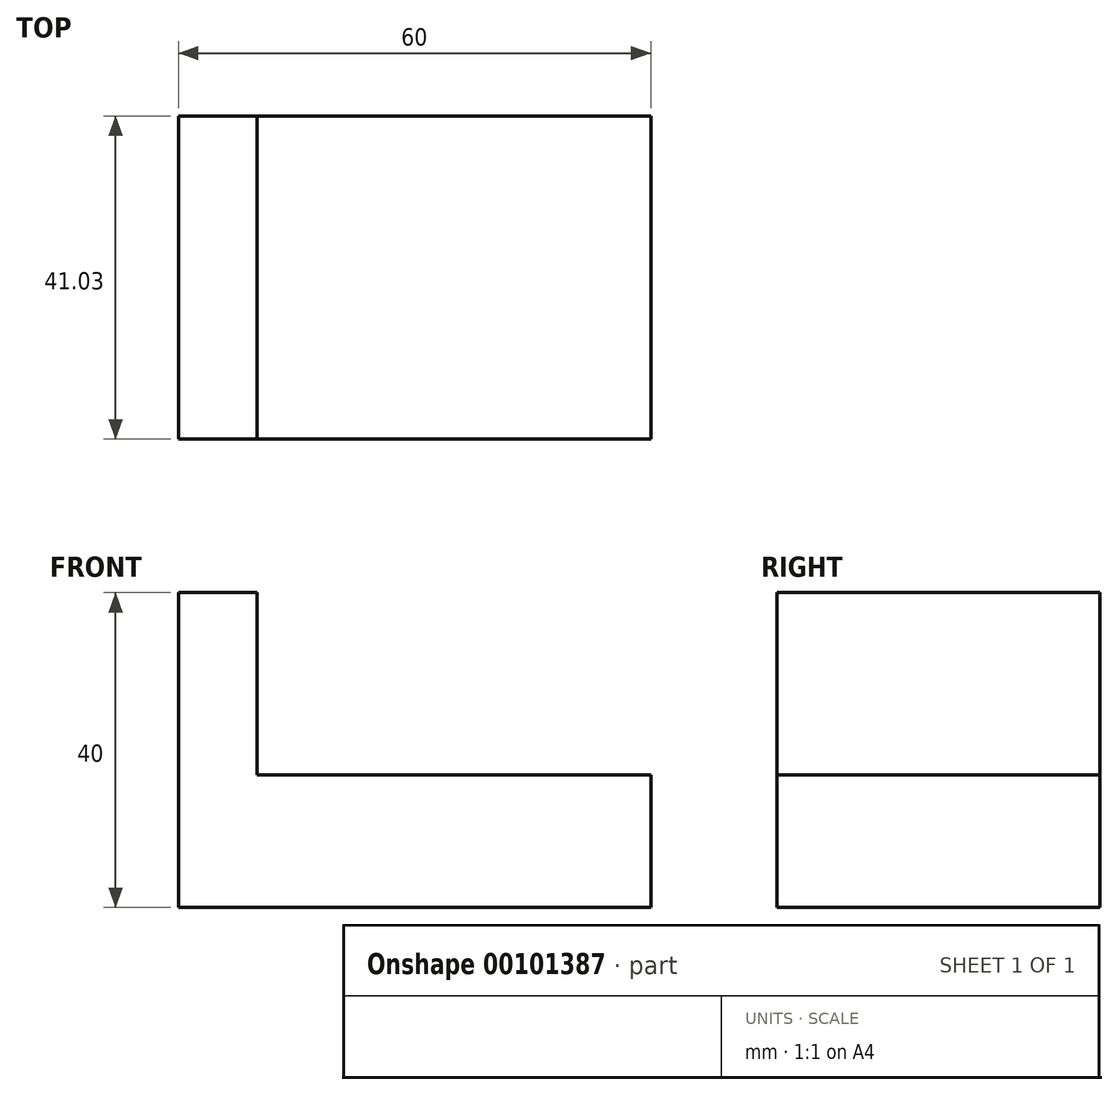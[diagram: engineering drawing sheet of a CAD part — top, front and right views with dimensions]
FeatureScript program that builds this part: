
annotation { "Feature Type Name" : "Feature", "Feature Type Description" : "" }
export const myFeature = defineFeature(function(context is Context, id is Id, definition is map)
    precondition{}
    {
        {
            var Q0;
            Q0=qCreatedBy(makeId("Front.planeOp"),FACE);
            var sketch = newSketch(context, id + "F0", { "sketchPlane" : qUnion([Q0])});
            skLineSegment(sketch, "E0", {"start": v(0, 0) * mm, "end": v(0, 40) * mm});
            skLineSegment(sketch, "E1", {"start": v(0, 40) * mm, "end": v(10, 40) * mm});
            skLineSegment(sketch, "E2", {"start": v(10, 40) * mm, "end": v(10, 16.82) * mm});
            skLineSegment(sketch, "E3", {"start": v(10, 16.82) * mm, "end": v(60, 16.82) * mm});
            skLineSegment(sketch, "E4", {"start": v(60, 16.82) * mm, "end": v(60, 0) * mm});
            skLineSegment(sketch, "E5", {"start": v(60, 0) * mm, "end": v(0, 0) * mm});
            skSolve(sketch);
        }
        {
            var Q0;
            Q0 = qSketchRegion(id + "F0", true);
            extrude(context, id + "F1", {"entities" : qUnion([Q0]), "depth" : 41.03 * mm});
        }
    });
